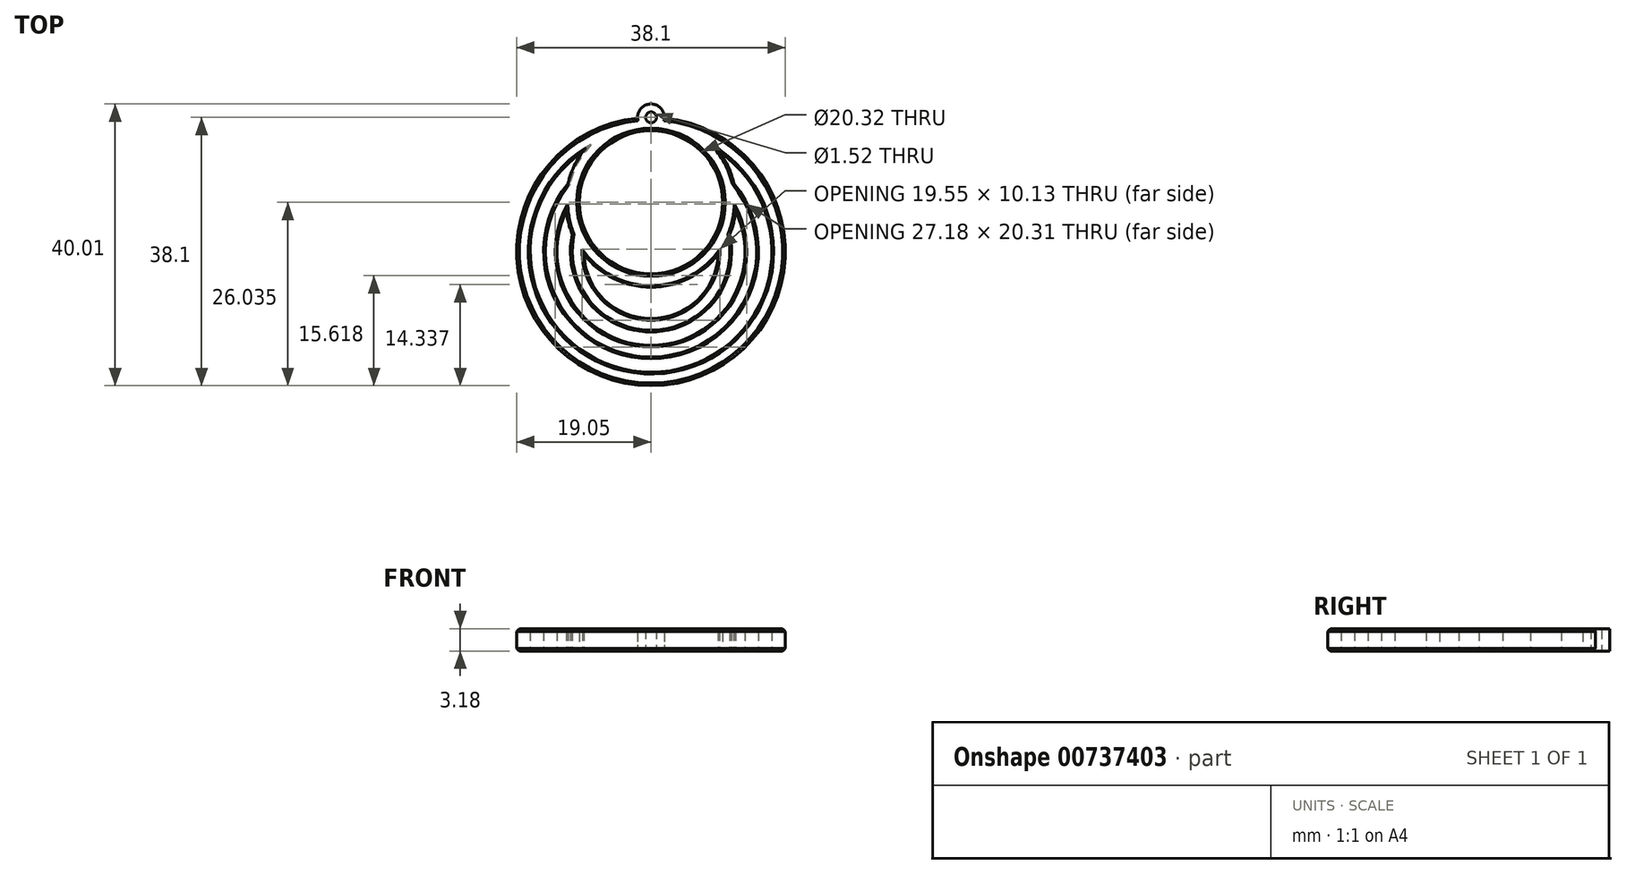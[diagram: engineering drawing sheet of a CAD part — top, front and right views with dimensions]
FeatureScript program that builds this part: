
annotation { "Feature Type Name" : "Feature", "Feature Type Description" : "" }
export const myFeature = defineFeature(function(context is Context, id is Id, definition is map)
    precondition{}
    {
        {
            var Q0;
            Q0=qCreatedBy(makeId("Top.planeOp"),FACE);
            var sketch = newSketch(context, id + "F0", { "sketchPlane" : qUnion([Q0])});
            skArc(sketch, "E0", {"start": v(-1.9, 18.95) * mm, "mid": v(0, -19.05) * mm, "end": v(1.9, 18.95) * mm});
            skCircle(sketch, "E1", {"center": v(0, 6.98) * mm, "radius": 10.16 * mm});
            skArc(sketch, "E2.0", {"start": v(-9.73, 14.11) * mm, "mid": v(0, -17.14) * mm, "end": v(9.73, 14.11) * mm});
            skArc(sketch, "E3.0", {"start": v(-11.76, 9.7) * mm, "mid": v(0, -15.24) * mm, "end": v(11.76, 9.7) * mm});
            skArc(sketch, "E4.0", {"start": v(-12, 5.8) * mm, "mid": v(0, -13.33) * mm, "end": v(12, 5.8) * mm});
            skArc(sketch, "E5.0", {"start": v(-11.17, 2.42) * mm, "mid": v(0, -11.43) * mm, "end": v(11.17, 2.42) * mm});
            skArc(sketch, "E6.0", {"start": v(-9.52, -0.43) * mm, "mid": v(0, -9.52) * mm, "end": v(9.52, -0.43) * mm});
            skArc(sketch, "E7.0", {"start": v(-9.73, 14.11) * mm, "mid": v(-10.97, 12) * mm, "end": v(-11.76, 9.7) * mm});
            skArc(sketch, "E8.trimOffspring", {"start": v(-12, 5.8) * mm, "mid": v(-11.71, 4.08) * mm, "end": v(-11.17, 2.42) * mm});
            skArc(sketch, "E9.trimOffspring", {"start": v(-9.52, -0.43) * mm, "mid": v(-8.39, -1.69) * mm, "end": v(-7.1, -2.77) * mm});
            skArc(sketch, "E10.trimOffspring", {"start": v(-7.1, -2.77) * mm, "mid": v(0, -5.08) * mm, "end": v(7.1, -2.77) * mm});
            skArc(sketch, "E11.trimOffspring", {"start": v(7.1, -2.77) * mm, "mid": v(8.39, -1.69) * mm, "end": v(9.52, -0.43) * mm});
            skArc(sketch, "E12.trimOffspring", {"start": v(11.17, 2.42) * mm, "mid": v(11.71, 4.08) * mm, "end": v(12, 5.8) * mm});
            skArc(sketch, "E13.trimOffspring", {"start": v(11.76, 9.7) * mm, "mid": v(10.97, 12) * mm, "end": v(9.73, 14.11) * mm});
            skCircle(sketch, "E14", {"center": v(0, 19.05) * mm, "radius": 0.76 * mm});
            skArc(sketch, "E15", {"start": v(1.9, 18.95) * mm, "mid": v(0, 20.96) * mm, "end": v(-1.9, 18.95) * mm});
            skSolve(sketch);
        }
        {
            var Q0;
            Q0=makeQuery(id+"F0.imprint","IMPRINT",FACE,{"disambiguationData":[TD([[makeQuery(id+"F0.imprint","IMPRINT",EDGE,{"derivedFrom":sQuery(id+"F0.wireOp",EDGE,"E0")}),1.0]])]});
            extrude(context, id + "F1", {"entities" : qUnion([Q0]), "depth" : 3.17 * mm, "offsetDistance" : 25.4 * mm});
        }
        {
            var Q0;
            Q0=makeQuery(id+"F1.opExtrude","CAP_EDGE",EDGE,{"disambiguationData":[OSD([sQuery(id+"F0.wireOp",EDGE,"E0")])],"isStart":false});
            var Q1;
            Q1=makeQuery(id+"F1.opExtrude","CAP_EDGE",EDGE,{"disambiguationData":[OSD([sQuery(id+"F0.wireOp",EDGE,"E1")])],"isStart":false});
            var Q2;
            Q2=makeQuery(id+"F1.opExtrude","CAP_EDGE",EDGE,{"disambiguationData":[OSD([sQuery(id+"F0.wireOp",EDGE,"E0")])],"isStart":true});
            var Q3;
            Q3=makeQuery(id+"F1.opExtrude","CAP_EDGE",EDGE,{"disambiguationData":[OSD([sQuery(id+"F0.wireOp",EDGE,"E1")])],"isStart":true});
            chamfer(context, id + "F2", {"entities" : qUnion([Q0, Q1, Q2, Q3]), "width" : 0.38 * mm, "tangentPropagation" : true});
        }
        {
            var Q0;
            Q0=makeQuery(id+"F1.opExtrude","CAP_EDGE",EDGE,{"disambiguationData":[OSD([sQuery(id+"F0.wireOp",EDGE,"E2.0")])],"isStart":false});
            var Q1;
            Q1=makeQuery(id+"F1.opExtrude","CAP_EDGE",EDGE,{"disambiguationData":[OSD([sQuery(id+"F0.wireOp",EDGE,"E4.0")])],"isStart":false});
            var Q2;
            Q2=makeQuery(id+"F1.opExtrude","CAP_EDGE",EDGE,{"disambiguationData":[OSD([sQuery(id+"F0.wireOp",EDGE,"E6.0")])],"isStart":false});
            var Q3;
            Q3=makeQuery(id+"F1.opExtrude","CAP_EDGE",EDGE,{"disambiguationData":[OSD([sQuery(id+"F0.wireOp",EDGE,"E3.0")])],"isStart":false});
            var Q4;
            Q4=makeQuery(id+"F1.opExtrude","CAP_EDGE",EDGE,{"disambiguationData":[OSD([sQuery(id+"F0.wireOp",EDGE,"E5.0")])],"isStart":false});
            var Q5;
            Q5=makeQuery(id+"F1.opExtrude","CAP_EDGE",EDGE,{"disambiguationData":[OSD([sQuery(id+"F0.wireOp",EDGE,"E9.trimOffspring"),sQuery(id+"F0.wireOp",EDGE,"E10.trimOffspring"),sQuery(id+"F0.wireOp",EDGE,"E11.trimOffspring")])],"isStart":false});
            var Q6;
            Q6=makeQuery(id+"F1.opExtrude","CAP_EDGE",EDGE,{"disambiguationData":[OSD([sQuery(id+"F0.wireOp",EDGE,"E2.0")])],"isStart":true});
            var Q7;
            Q7=makeQuery(id+"F1.opExtrude","CAP_EDGE",EDGE,{"disambiguationData":[OSD([sQuery(id+"F0.wireOp",EDGE,"E4.0")])],"isStart":true});
            var Q8;
            Q8=makeQuery(id+"F1.opExtrude","CAP_EDGE",EDGE,{"disambiguationData":[OSD([sQuery(id+"F0.wireOp",EDGE,"E6.0")])],"isStart":true});
            var Q9;
            Q9=makeQuery(id+"F1.opExtrude","CAP_EDGE",EDGE,{"disambiguationData":[OSD([sQuery(id+"F0.wireOp",EDGE,"E5.0")])],"isStart":true});
            var Q10;
            Q10=makeQuery(id+"F1.opExtrude","CAP_EDGE",EDGE,{"disambiguationData":[OSD([sQuery(id+"F0.wireOp",EDGE,"E9.trimOffspring"),sQuery(id+"F0.wireOp",EDGE,"E10.trimOffspring"),sQuery(id+"F0.wireOp",EDGE,"E11.trimOffspring")])],"isStart":true});
            var Q11;
            Q11=makeQuery(id+"F1.opExtrude","CAP_EDGE",EDGE,{"disambiguationData":[OSD([sQuery(id+"F0.wireOp",EDGE,"E3.0")])],"isStart":true});
            var Q12;
            Q12=makeQuery(id+"F1.opExtrude","CAP_EDGE",EDGE,{"disambiguationData":[OSD([sQuery(id+"F0.wireOp",EDGE,"E12.trimOffspring")])],"isStart":true});
            var Q13;
            Q13=makeQuery(id+"F1.opExtrude","CAP_EDGE",EDGE,{"disambiguationData":[OSD([sQuery(id+"F0.wireOp",EDGE,"E13.trimOffspring")])],"isStart":true});
            var Q14;
            Q14=makeQuery(id+"F1.opExtrude","CAP_EDGE",EDGE,{"disambiguationData":[OSD([sQuery(id+"F0.wireOp",EDGE,"E7.0")])],"isStart":true});
            var Q15;
            Q15=makeQuery(id+"F1.opExtrude","CAP_EDGE",EDGE,{"disambiguationData":[OSD([sQuery(id+"F0.wireOp",EDGE,"E8.trimOffspring")])],"isStart":true});
            var Q16;
            Q16=makeQuery(id+"F1.opExtrude","CAP_EDGE",EDGE,{"disambiguationData":[OSD([sQuery(id+"F0.wireOp",EDGE,"E8.trimOffspring")])],"isStart":false});
            var Q17;
            Q17=makeQuery(id+"F1.opExtrude","CAP_EDGE",EDGE,{"disambiguationData":[OSD([sQuery(id+"F0.wireOp",EDGE,"E13.trimOffspring")])],"isStart":false});
            var Q18;
            Q18=makeQuery(id+"F1.opExtrude","CAP_EDGE",EDGE,{"disambiguationData":[OSD([sQuery(id+"F0.wireOp",EDGE,"E12.trimOffspring")])],"isStart":false});
            chamfer(context, id + "F3", {"entities" : qUnion([Q0, Q1, Q2, Q3, Q4, Q5, Q6, Q7, Q8, Q9, Q10, Q11, Q12, Q13, Q14, Q15, Q16, Q17, Q18]), "width" : 0.25 * mm, "tangentPropagation" : true});
        }
    });
